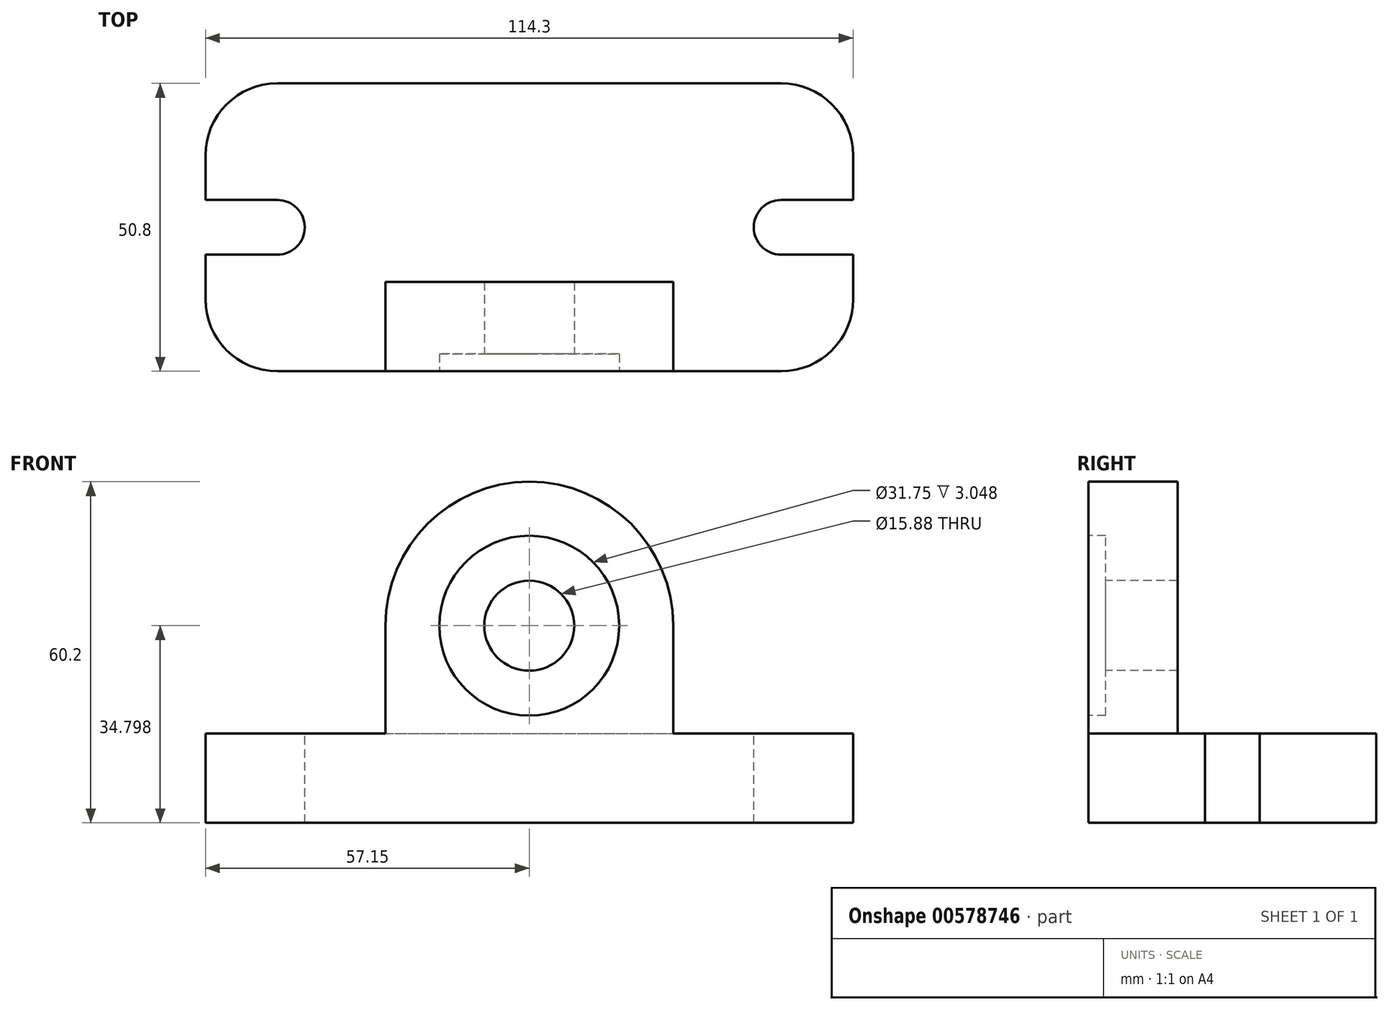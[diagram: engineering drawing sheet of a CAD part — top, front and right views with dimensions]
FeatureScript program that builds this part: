
annotation { "Feature Type Name" : "Feature", "Feature Type Description" : "" }
export const myFeature = defineFeature(function(context is Context, id is Id, definition is map)
    precondition{}
    {
        {
            var Q0;
            Q0=qCreatedBy(makeId("Top.planeOp"),FACE);
            var sketch = newSketch(context, id + "F0", { "sketchPlane" : qUnion([Q0])});
            skLineSegment(sketch, "E0.bottom", {"start": v(-57.15, 25.4) * mm, "end": v(57.15, 25.4) * mm});
            skLineSegment(sketch, "E0.top", {"start": v(-57.15, -25.4) * mm, "end": v(57.15, -25.4) * mm});
            skLineSegment(sketch, "E0.left", {"start": v(-57.15, 25.4) * mm, "end": v(-57.15, -25.4) * mm});
            skLineSegment(sketch, "E0.right", {"start": v(57.15, 25.4) * mm, "end": v(57.15, -25.4) * mm});
            skPoint(sketch, "E0.middle", {"position": v(0, 0) * mm});
            skSolve(sketch);
        }
        {
            var Q0;
            Q0 = qSketchRegion(id + "F0", true);
            var Q1;
            Q1=makeQuery(id+"F0.imprint","IMPRINT",FACE,{"disambiguationData":[TD([[makeQuery(id+"F0.imprint","IMPRINT",EDGE,{"derivedFrom":sQuery(id+"F0.wireOp",EDGE,"E0.bottom")}),-1.0]])]});
            extrude(context, id + "F1", {"entities" : qUnion([Q0, Q1]), "depth" : 15.75 * mm, "offsetDistance" : 25.4 * mm});
        }
        {
            var Q0;
            Q0=makeQuery(id+"F1.opExtrude","SWEPT_FACE",FACE,{"disambiguationData":[OSD([sQuery(id+"F0.wireOp",EDGE,"E0.top")])]});
            var sketch = newSketch(context, id + "F2", { "sketchPlane" : qUnion([Q0])});
            skPoint(sketch, "E1", {"position": v(0, 34.8) * mm});
            skPoint(sketch, "E1.positionSnap0", {"position": v(0, 15.75) * mm});
            skArc(sketch, "E2", {"start": v(25.4, 34.8) * mm, "mid": v(0, 60.2) * mm, "end": v(-25.4, 34.8) * mm});
            skCircle(sketch, "E3", {"center": v(0, 34.8) * mm, "radius": 15.88 * mm});
            skCircle(sketch, "E4", {"center": v(0, 34.8) * mm, "radius": 7.94 * mm});
            skLineSegment(sketch, "E5", {"start": v(-25.4, 34.8) * mm, "end": v(-25.4, 15.75) * mm});
            skLineSegment(sketch, "E6", {"start": v(25.4, 34.8) * mm, "end": v(25.4, 15.75) * mm});
            skSolve(sketch);
        }
        {
            var Q0;
            Q0=makeQuery(id+"F2.imprint","IMPRINT",FACE,{"disambiguationData":[TD([[makeQuery(id+"F2.imprint","IMPRINT",EDGE,{"derivedFrom":sQuery(id+"F2.wireOp",EDGE,"E2")}),1.0]])]});
            var Q1;
            Q1=makeQuery(id+"F2.imprint","IMPRINT",FACE,{"disambiguationData":[TD([[makeQuery(id+"F2.imprint","IMPRINT",EDGE,{"derivedFrom":sQuery(id+"F2.wireOp",EDGE,"E4")}),1.0]])]});
            var Q2;
            Q2=makeQuery(id+"F2.imprint","IMPRINT",FACE,{"disambiguationData":[TD([[makeQuery(id+"F2.imprint","IMPRINT",EDGE,{"derivedFrom":sQuery(id+"F2.wireOp",EDGE,"E3")}),1.0]])]});
            extrude(context, id + "F3", {"entities" : qUnion([Q0, Q1, Q2]), "operationType" : NewBodyOperationType.ADD, "oppositeDirection" : true, "depth" : 15.75 * mm, "offsetDistance" : 25.4 * mm});
        }
        {
            var Q0;
            Q0=makeQuery(id+"F2.imprint","IMPRINT",FACE,{"disambiguationData":[TD([[makeQuery(id+"F2.imprint","IMPRINT",EDGE,{"derivedFrom":sQuery(id+"F2.wireOp",EDGE,"E3")}),1.0]])]});
            extrude(context, id + "F4", {"entities" : qUnion([Q0]), "operationType" : NewBodyOperationType.REMOVE, "oppositeDirection" : true, "depth" : 3.05 * mm, "offsetDistance" : 25.4 * mm});
        }
        {
            var Q0;
            Q0=makeQuery(id+"F2.imprint","IMPRINT",FACE,{"disambiguationData":[TD([[makeQuery(id+"F2.imprint","IMPRINT",EDGE,{"derivedFrom":sQuery(id+"F2.wireOp",EDGE,"E4")}),1.0]])]});
            extrude(context, id + "F5", {"entities" : qUnion([Q0]), "operationType" : NewBodyOperationType.REMOVE, "endBound" : BoundingType.THROUGH_ALL, "oppositeDirection" : true, "depth" : 25.4 * mm, "offsetDistance" : 25.4 * mm});
        }
        {
            var Q0;
            Q0=makeQuery(id+"F1.opExtrude","CAP_FACE",FACE,{"disambiguationData":[OSD([sQuery(id+"F0.wireOp",EDGE,"E0.bottom"),sQuery(id+"F0.wireOp",EDGE,"E0.top"),sQuery(id+"F0.wireOp",EDGE,"E0.left"),sQuery(id+"F0.wireOp",EDGE,"E0.right")])],"isStart":false});
            var sketch = newSketch(context, id + "F6", { "sketchPlane" : qUnion([Q0])});
            skPoint(sketch, "E7", {"position": v(-44.45, 0) * mm});
            skArc(sketch, "E8", {"start": v(-44.45, -4.83) * mm, "mid": v(-39.62, 0) * mm, "end": v(-44.45, 4.83) * mm});
            skLineSegment(sketch, "E9", {"start": v(-44.45, 4.83) * mm, "end": v(-57.15, 4.83) * mm});
            skLineSegment(sketch, "E10", {"start": v(-44.45, -4.83) * mm, "end": v(-57.15, -4.83) * mm});
            skPoint(sketch, "E11.start.orphan", {"position": v(-57.15, 0) * mm});
            skLineSegment(sketch, "E12", {"start": v(0, 7.38) * mm, "end": v(0, -5.23) * mm, "construction": true});
            skLineSegment(sketch, "E13.MirrorCS", {"start": v(44.45, 4.83) * mm, "end": v(57.15, 4.83) * mm});
            skArc(sketch, "E14.MirrorCS", {"start": v(44.45, -4.83) * mm, "mid": v(39.62, 0) * mm, "end": v(44.45, 4.83) * mm});
            skLineSegment(sketch, "E15.MirrorCS", {"start": v(44.45, -4.83) * mm, "end": v(57.15, -4.83) * mm});
            skSolve(sketch);
        }
        {
            var Q0;
            Q0=makeQuery(id+"F6.imprint","IMPRINT",FACE,{"disambiguationData":[TD([[makeQuery(id+"F6.imprint","IMPRINT",EDGE,{"derivedFrom":sQuery(id+"F6.wireOp",EDGE,"E8")}),1.0]])]});
            var Q1;
            {var subQ0=sQuery(id+"F6.wireOp",EDGE,"E13.MirrorCS");Q1=makeQuery(id+"F6.imprint","IMPRINT",FACE,{"disambiguationData":[TD([[makeQuery(id+"F6.imprint","IMPRINT",EDGE,{"derivedFrom":subQ0}),-1.0]])]});}
            extrude(context, id + "F7", {"entities" : qUnion([Q0, Q1]), "operationType" : NewBodyOperationType.REMOVE, "endBound" : BoundingType.THROUGH_ALL, "oppositeDirection" : true, "depth" : 25.4 * mm, "offsetDistance" : 25.4 * mm});
        }
        {
            var Q0;
            Q0=makeQuery(id+"F1.opExtrude","SWEPT_EDGE",EDGE,{"disambiguationData":[OSD([sQuery(id+"F0.wireOp",EDGE,"E0.top"),sQuery(id+"F0.wireOp",EDGE,"E0.right")])]});
            var Q1;
            Q1=makeQuery(id+"F1.opExtrude","SWEPT_EDGE",EDGE,{"disambiguationData":[OSD([sQuery(id+"F0.wireOp",EDGE,"E0.bottom"),sQuery(id+"F0.wireOp",EDGE,"E0.right")])]});
            var Q2;
            Q2=makeQuery(id+"F1.opExtrude","SWEPT_EDGE",EDGE,{"disambiguationData":[OSD([sQuery(id+"F0.wireOp",EDGE,"E0.top"),sQuery(id+"F0.wireOp",EDGE,"E0.left")])]});
            var Q3;
            Q3=makeQuery(id+"F1.opExtrude","SWEPT_EDGE",EDGE,{"disambiguationData":[OSD([sQuery(id+"F0.wireOp",EDGE,"E0.bottom"),sQuery(id+"F0.wireOp",EDGE,"E0.left")])]});
            fillet(context, id + "F8", {"entities" : qUnion([Q0, Q1, Q2, Q3]), "radius" : 12.7 * mm, "tangentPropagation" : true, "allowEdgeOverflow" : false});
        }
    });
